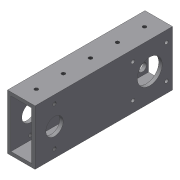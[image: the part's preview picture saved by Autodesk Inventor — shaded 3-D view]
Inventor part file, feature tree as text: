
AUTODESK INVENTOR PART (.ipt)
format: ipt  version: 2018 (Build 220112000, 112)  size: 160,768 bytes
history: native  units: mm
features: sketch x6, hole x4, extrude x3, other x3, shell x1, pattern_linear x1, reference x1
ambient origin geometry x8: Origin, YZ Plane, XZ Plane, XY Plane, X Axis, Y Axis, Z Axis, Center Point
bodies: Solid1 (feature_tree)
feature tree (19):
  extrude  "Extrusion1"  Depth=25.4mm
  shell  "Shell1"  Thickness=127.0mm
  sketch  "Sketch2"  dims[d4=3.175mm d5=31.0mm]
  hole  "Hole1"  [1 undecoded]
  hole  "Hole2"  [1 undecoded]
  extrude  "Extrusion2"  Depth=8.0mm
  extrude  "Extrusion3"  Depth=50.8mm
  hole  "Hole4"  [1 undecoded]
  hole  "Hole5"  [1 undecoded]
  pattern_linear  "Rectangular Pattern1"  Spacing1=36.0mm  [1 undecoded]
  sketch  "Sketch1"  dims[d0=50.8mm d1=25.4mm d2=127.0mm d3=0.0mm]
  sketch  "Sketch3"  dims[d6=31.0mm d7=21.0mm]
  sketch  "Sketch4"  dims[d8=3.2mm d9=6.0mm d10=7.5mm d11=5.0mm d12=90.0deg d13=8.0mm d14=20.594885mm]
  sketch  "Sketch6"  dims[d15=10.0mm d16=6.0mm d17=6.5mm d18=3.0mm d19=90.0deg d20=8.0mm d21=20.594885mm d22=23.0mm]
  sketch  "Sketch7"  dims[d23=50.8mm d24=0.0mm d25=16.0mm d26=18.0mm d27=50.8mm d28=0.0mm d40=3.242mm d41=100.0mm d42=6.5mm d43=3.0mm d44=90.0deg d45=11.8mm d46=20.594885mm d47=36.0mm d48=3.242mm d49=100.0mm d50=6.5mm d51=3.0mm d52=90.0deg d53=11.8mm d54=20.594885mm d55=50.0mm d57=20.0mm d59=50.0mm d61=38.1mm]
  reference  "Reference1"
  parser-record x1  (decoder bookkeeping rows leaked as tree rows — omitted from the tree; the rows remain in map.json)
  other  "AMR_Transm2.iam"
  other  "7804K147_STAINLESS STEEL BALL BEARING:2"
note: 5 required parameter values undecoded (feature->parameter linkage not recoverable at this tier; creation-order binding heuristic only, values carry confidence <= 0.55)
note: 1 file-system path scrubbed to <path> (originals preserved in map.json)
